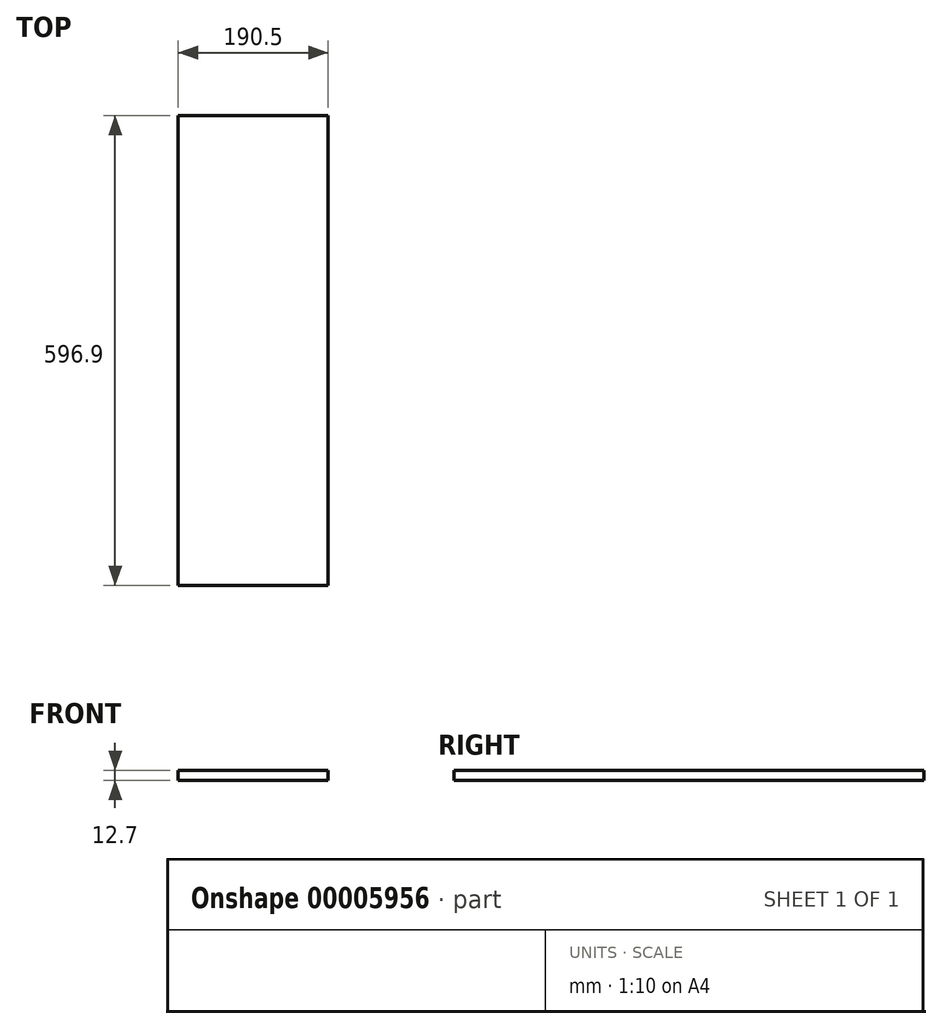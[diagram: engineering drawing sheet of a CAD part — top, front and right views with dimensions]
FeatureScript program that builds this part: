
annotation { "Feature Type Name" : "Feature", "Feature Type Description" : "" }
export const myFeature = defineFeature(function(context is Context, id is Id, definition is map)
    precondition{}
    {
        {
            var Q0;
            Q0=qCreatedBy(makeId("Top.planeOp"),FACE);
            var sketch = newSketch(context, id + "F0", { "sketchPlane" : qUnion([Q0])});
            skLineSegment(sketch, "E0.bottom", {"start": v(-418.93, 289.58) * mm, "end": v(-228.43, 289.58) * mm});
            skLineSegment(sketch, "E0.top", {"start": v(-418.93, -307.32) * mm, "end": v(-228.43, -307.32) * mm});
            skLineSegment(sketch, "E0.left", {"start": v(-418.93, 289.58) * mm, "end": v(-418.93, -307.32) * mm});
            skLineSegment(sketch, "E0.right", {"start": v(-228.43, 289.58) * mm, "end": v(-228.43, -307.32) * mm});
            skSolve(sketch);
        }
        {
            var Q0;
            Q0=makeQuery(id+"F0.imprint","IMPRINT",FACE,{"disambiguationData":[TD([[makeQuery(id+"F0.imprint","IMPRINT",EDGE,{"derivedFrom":sQuery(id+"F0.wireOp",EDGE,"E0.bottom")}),-1.0]])]});
            extrude(context, id + "F1", {"entities" : qUnion([Q0]), "depth" : 12.7 * mm});
        }
    });
